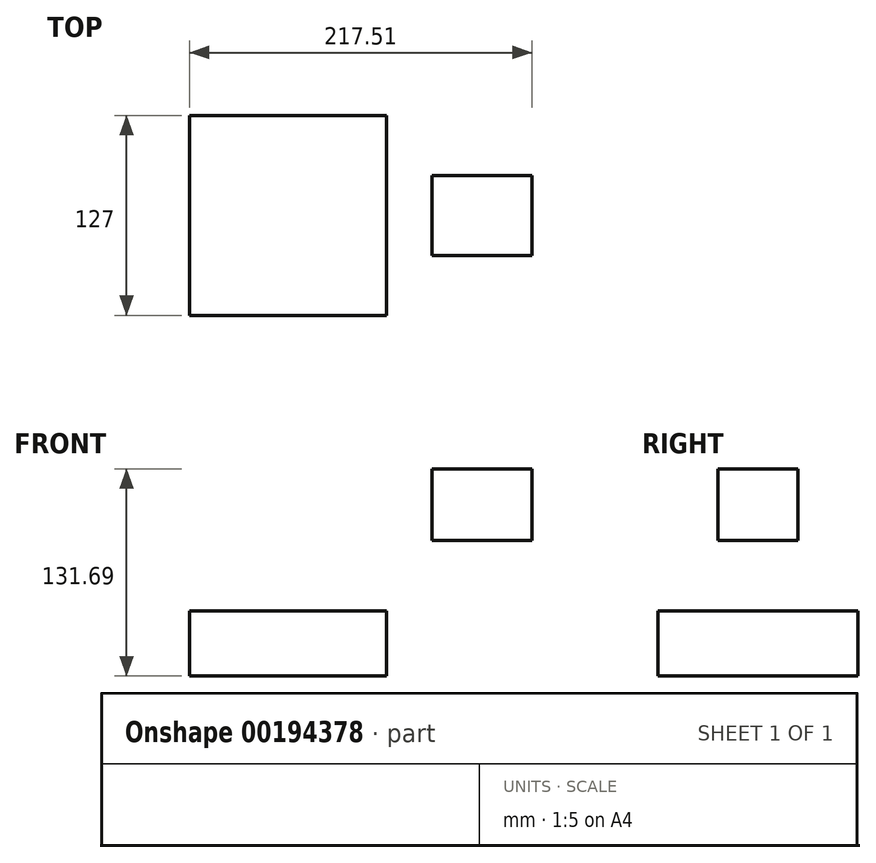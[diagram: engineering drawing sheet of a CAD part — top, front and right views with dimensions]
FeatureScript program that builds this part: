
annotation { "Feature Type Name" : "Feature", "Feature Type Description" : "" }
export const myFeature = defineFeature(function(context is Context, id is Id, definition is map)
    precondition{}
    {
        {
            var Q0;
            Q0=qCreatedBy(makeId("Front.planeOp"),FACE);
            var sketch = newSketch(context, id + "F0", { "sketchPlane" : qUnion([Q0])});
            skLineSegment(sketch, "E0.bottom", {"start": v(-62.48, -31.11) * mm, "end": v(62.48, -31.11) * mm});
            skLineSegment(sketch, "E0.top", {"start": v(-62.48, 10.37) * mm, "end": v(62.48, 10.37) * mm});
            skLineSegment(sketch, "E0.left", {"start": v(-62.48, -31.11) * mm, "end": v(-62.48, 10.37) * mm});
            skLineSegment(sketch, "E0.right", {"start": v(62.48, -31.11) * mm, "end": v(62.48, 10.37) * mm});
            skPoint(sketch, "E0.middle", {"position": v(0, -10.37) * mm});
            skLineSegment(sketch, "E1.bottom", {"start": v(91.38, 55.04) * mm, "end": v(155.03, 55.04) * mm});
            skLineSegment(sketch, "E1.top", {"start": v(91.38, 100.58) * mm, "end": v(155.03, 100.58) * mm});
            skLineSegment(sketch, "E1.left", {"start": v(91.38, 55.04) * mm, "end": v(91.38, 100.58) * mm});
            skLineSegment(sketch, "E1.right", {"start": v(155.03, 55.04) * mm, "end": v(155.03, 100.58) * mm});
            skPoint(sketch, "E1.middle", {"position": v(123.2, 77.8) * mm});
            skLineSegment(sketch, "E2", {"start": v(62.48, 10.37) * mm, "end": v(62.48, 53.58) * mm});
            skArc(sketch, "E3", {"start": v(62.48, 53.58) * mm, "mid": v(65.7, 61.33) * mm, "end": v(73.45, 64.54) * mm});
            skLineSegment(sketch, "E4", {"start": v(73.45, 64.54) * mm, "end": v(125.15, 64.54) * mm});
            skLineSegment(sketch, "E5.0", {"start": v(73.45, 75.35) * mm, "end": v(125.15, 75.35) * mm});
            skArc(sketch, "E5.1", {"start": v(51.67, 53.58) * mm, "mid": v(58.05, 68.97) * mm, "end": v(73.45, 75.35) * mm});
            skLineSegment(sketch, "E5.2", {"start": v(51.67, 17.38) * mm, "end": v(51.67, 53.58) * mm});
            skLineSegment(sketch, "E6", {"start": v(125.15, 64.54) * mm, "end": v(125.15, 75.35) * mm});
            skSolve(sketch);
        }
        {
            var Q0;
            Q0=makeQuery(id+"F0.imprint","IMPRINT",FACE,{"disambiguationData":[TD([[makeQuery(id+"F0.imprint","IMPRINT",EDGE,{"derivedFrom":sQuery(id+"F0.wireOp",EDGE,"E0.bottom")}),1.0]])]});
            extrude(context, id + "F1", {"entities" : qUnion([Q0]), "endBound" : BoundingType.SYMMETRIC, "depth" : 127 * mm});
        }
        {
            var Q0;
            Q0 = qSketchRegion(id + "F0", true);
            extrude(context, id + "F2", {"entities" : qUnion([Q0]), "operationType" : NewBodyOperationType.ADD, "endBound" : BoundingType.SYMMETRIC, "depth" : 50.8 * mm});
        }
    });
